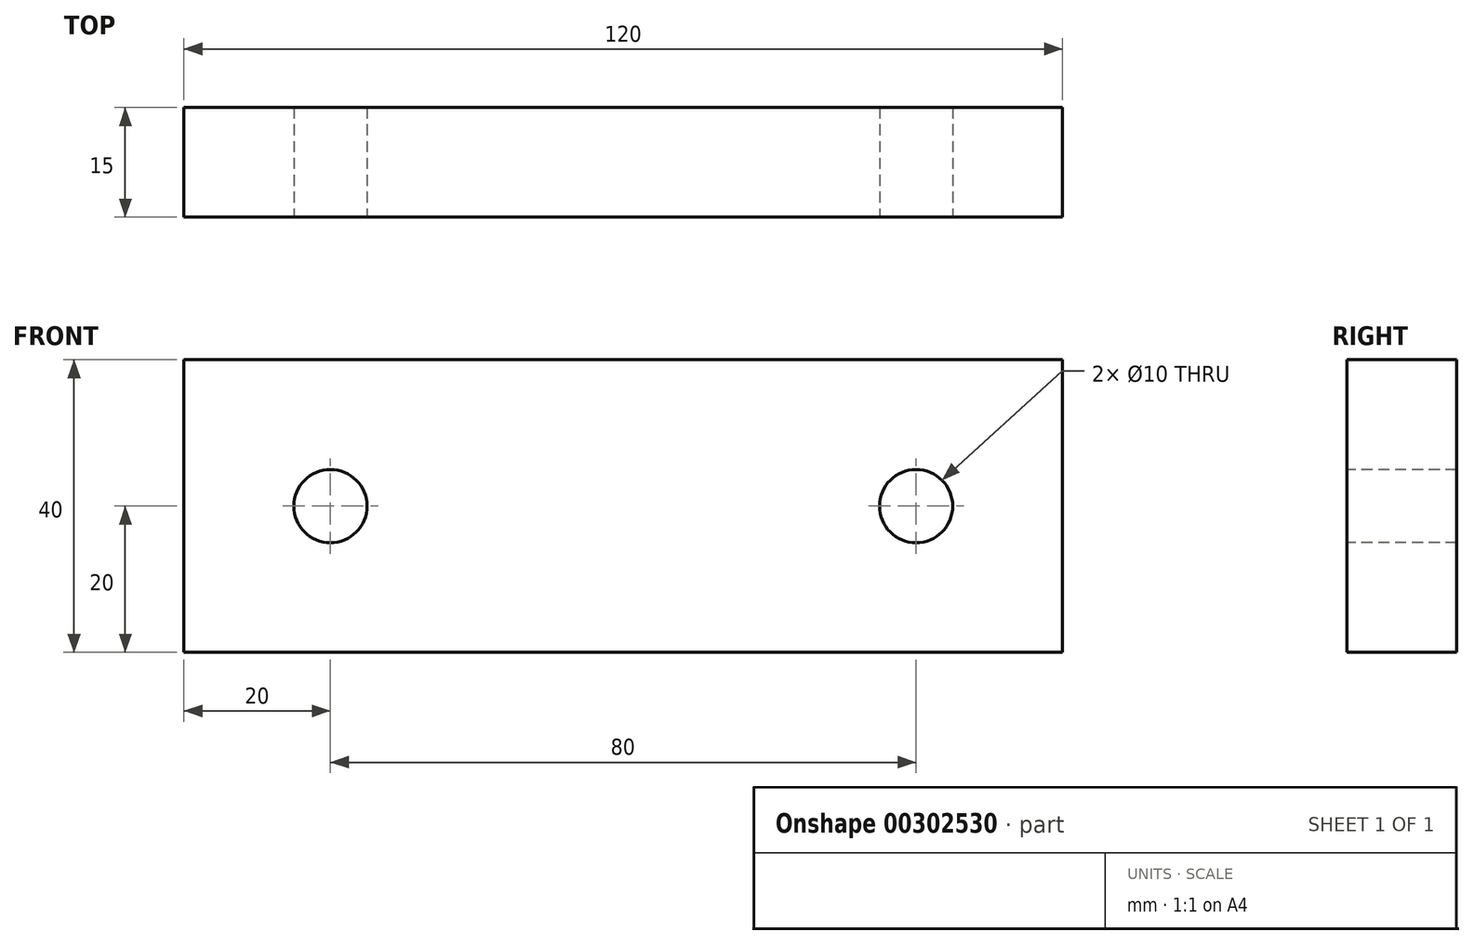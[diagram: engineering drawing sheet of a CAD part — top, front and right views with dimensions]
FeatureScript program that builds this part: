
annotation { "Feature Type Name" : "Feature", "Feature Type Description" : "" }
export const myFeature = defineFeature(function(context is Context, id is Id, definition is map)
    precondition{}
    {
        {
            var Q0;
            Q0=qCreatedBy(makeId("Front.planeOp"),FACE);
            var sketch = newSketch(context, id + "F0", { "sketchPlane" : qUnion([Q0])});
            skLineSegment(sketch, "E0", {"start": v(0, 0) * mm, "end": v(120, 0) * mm});
            skLineSegment(sketch, "E1", {"start": v(120, 0) * mm, "end": v(120, 40) * mm});
            skLineSegment(sketch, "E2", {"start": v(120, 40) * mm, "end": v(0, 40) * mm});
            skLineSegment(sketch, "E3", {"start": v(0, 40) * mm, "end": v(0, 0) * mm});
            skSolve(sketch);
        }
        {
            var Q0;
            Q0 = qSketchRegion(id + "F0", true);
            extrude(context, id + "F1", {"entities" : qUnion([Q0]), "endBound" : BoundingType.SYMMETRIC, "depth" : 15 * mm});
        }
        {
            var Q0;
            Q0=makeQuery(id+"F1.opExtrude","CAP_FACE",FACE,{"disambiguationData":[OSD([sQuery(id+"F0.wireOp",EDGE,"E0"),sQuery(id+"F0.wireOp",EDGE,"E1"),sQuery(id+"F0.wireOp",EDGE,"E2"),sQuery(id+"F0.wireOp",EDGE,"E3")])],"isStart":false});
            var sketch = newSketch(context, id + "F2", { "sketchPlane" : qUnion([Q0])});
            skCircle(sketch, "E4", {"center": v(20, 20) * mm, "radius": 5 * mm});
            skCircle(sketch, "E5", {"center": v(100, 20) * mm, "radius": 5 * mm});
            skSolve(sketch);
        }
        {
            var Q0;
            Q0 = qSketchRegion(id + "F2", true);
            extrude(context, id + "F3", {"entities" : qUnion([Q0]), "operationType" : NewBodyOperationType.REMOVE, "endBound" : BoundingType.SYMMETRIC, "oppositeDirection" : true, "depth" : 50 * mm});
        }
    });
